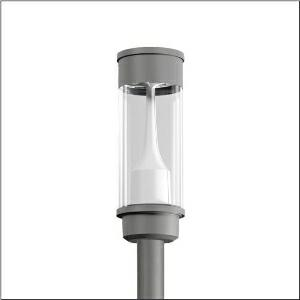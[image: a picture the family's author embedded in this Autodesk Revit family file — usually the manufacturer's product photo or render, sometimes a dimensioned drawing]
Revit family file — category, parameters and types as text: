
# Revit family: litepole_iq___pl1_2s_5xa5415jf14h_0c6a
name_source: partatom
category: Lighting Fixtures
units: mm (PartAtom-declared; Revit-internal decimal feet)

## family parameters
Cut with Voids When Loaded = No
Host = Face
Light Source = No
Part Type = Normal
Room Calculation Point = No
Round Connector Dimension = Use Diameter
Shared = No

## types (1)
- --- (1 x LED, 2970 lm, 19.3 W, 3000K)
    Apparent Load = 19 VA
    CIE Flux Codes = 23 62 94 96 100
    Color Rendering = 70
    Color Temperature = 3000K
    Default Elevation = 1800 mm
    Description = Litepole iQ, mast luminaire, Module 540 iQ-SR, primary light control with 3 zone facetted reflector, of plastic, silver coated, highly specular, structured, primary optical cover: cover, of PMMA, transparent, light distribution: PL1.2s, light emission: direct distribution, primary light characteristic: symmetric, installation type: post-top, LED, High Power LED, rated luminous flux: 2.970lm, luminous efficacy: 154lm/W, light colour: 730, colour temperature: 3000K, control gear: iQ Street-Remote, control: Auto-Match, Temp-Guard, Lumen-Switch, Night-Set, Smart-Wire, Light-Fading, Desk-Remote (wireless, voltage-free reading and setting of iQ features in the workshop via application-optimized NFC function/RFID function), optimised constant luminous flux control (CLO 2.0), Street-Remote, pre-setting: logarithmic dimming characteristic, with terminal, 6-pole, max. 2.5mm², mains connection: 230..240V, AC, 50/60Hz, start of lifetime: 19W, end of service life: 21W, reduction: 10W, luminaire housing, upper part, of glass-fibre reinforced polyester, coated, Siteco® metallic grey (DB 702S), diameter: 210mm, height: 590mm, spigot size: d x l = 76 x 70mm (post-top) | with reducer (optional accessory) 60 x 70mm, mounting height: 3..5m, post-top mast mounting element, of diecast aluminium, coated, Siteco® metallic grey (DB 702S), Module 540 iQ-SR, traffic white (RAL 9016), equipment: standard, protection rating (complete): IP65, insulation class (complete): insulation class II (safety insulation), certification: CE, ENEC, VDE, packaging unit: 1 piece

Light Distribution: PL1.2s
    Height = 590 mm
    Lamp = 1 x LED
    Lamp Light Flux = 2970 lm
    Lamp Power = 19.3 W
    Lamp count = 1
    Length = 220 mm
    Luminous efficacy = 154 lm/W
    Manufacturer = Siteco
    ModVariant = No
    Model = 5XA5415JF14H
    Number of Poles = 1
    OnlyDefault = Yes
    Power Factor = 1
    Product Name = Litepole iQ | PL1.2s
    Product group = mast luminaire | pylon top
    ProductGroupID = 6100
    Protection Class = Protection class II
    Protection Degree = IP 65
    RLX_Detail_Level = 1
    RLX_Emergency_Light_Flux = 0 lm
    RLX_Emergency_Type = 0
    RLX_Emergency_Type_DB = No
    RlxData = <blob elided: 39821 chars, md5=28b8343c>
    Socket = socket
    Standby Power = 0 W
    System Light Flux = 2970 lm
    System Power = 19 W
    Type Comments = factory setting: luminous flux: 100 % | dim-lin: 254 | 403 mA
    Type Image = l_1006025.jpg
    URL = http://relux.com
    VarID = @adj_142258
    Voltage = 0 V
    Weight = 0.00 kg
    Width = 0 mm  [stored 0 ft]

note: [stored X ft] marks values corroborated as IEEE doubles in the binary element streams (Revit-internal decimal feet)

## geometry (parser evidence)
native form markers: Blend x4, Sweep x12
no freeform markers — native parametric forms only
